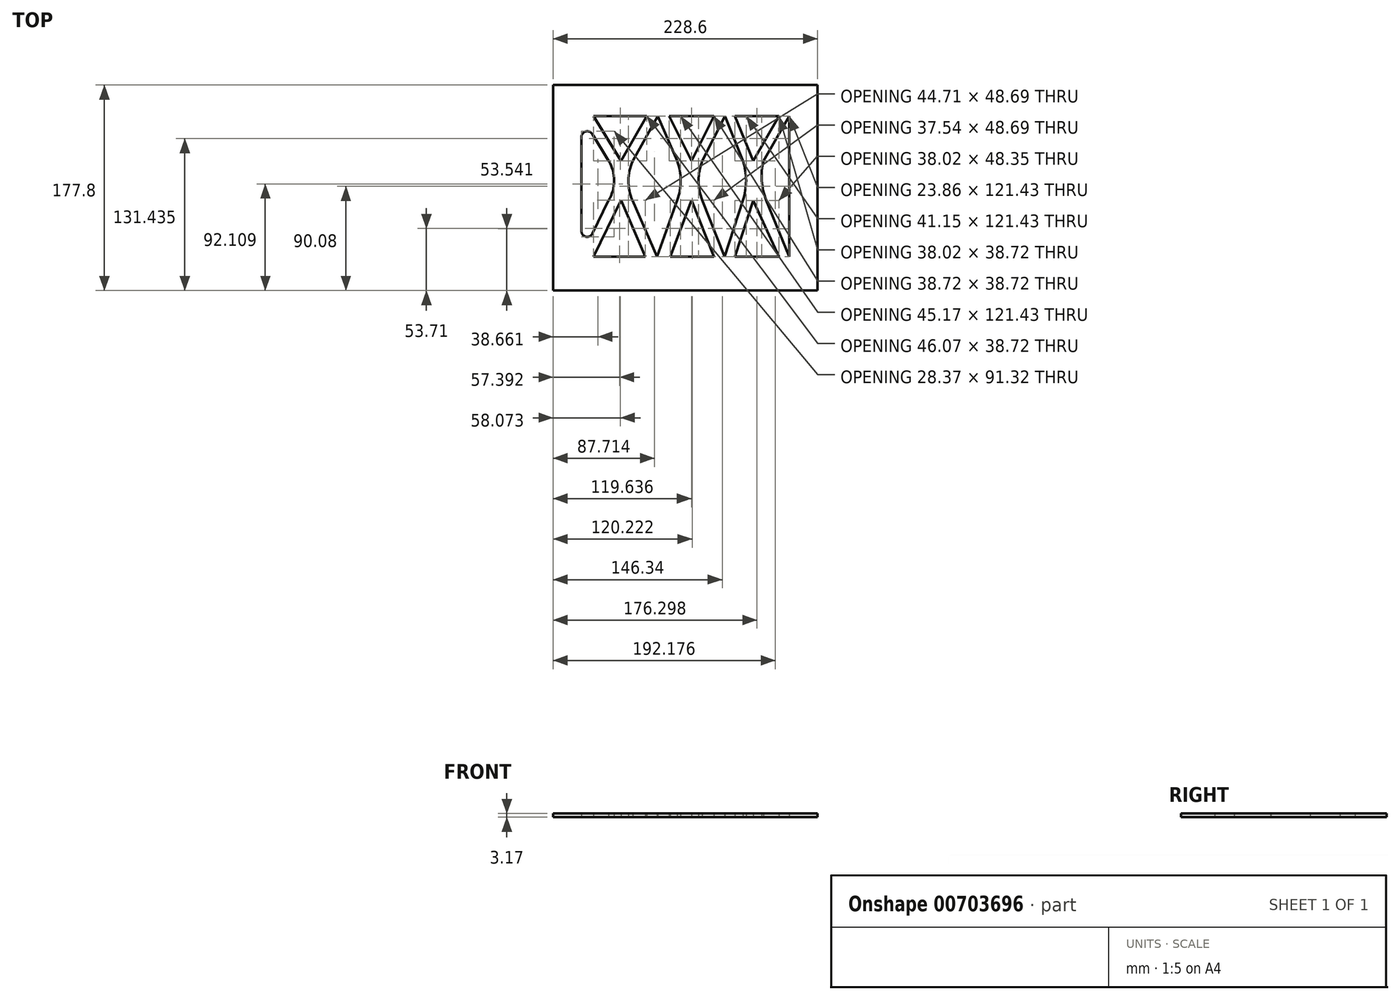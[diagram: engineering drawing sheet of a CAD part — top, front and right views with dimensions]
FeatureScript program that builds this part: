
annotation { "Feature Type Name" : "Feature", "Feature Type Description" : "" }
export const myFeature = defineFeature(function(context is Context, id is Id, definition is map)
    precondition{}
    {
        {
            var Q0;
            Q0=qCreatedBy(makeId("Top.planeOp"),FACE);
            var sketch = newSketch(context, id + "F0", { "sketchPlane" : qUnion([Q0])});
            skLineSegment(sketch, "E0", {"start": v(-115.17, 85) * mm, "end": v(-115.17, -92.8) * mm});
            skLineSegment(sketch, "E1", {"start": v(113.43, -92.8) * mm, "end": v(-115.17, -92.8) * mm});
            skLineSegment(sketch, "E2", {"start": v(113.43, -92.8) * mm, "end": v(113.43, 85) * mm});
            skLineSegment(sketch, "E3", {"start": v(113.43, 85) * mm, "end": v(-115.17, 85) * mm});
            skLineSegment(sketch, "E4", {"start": v(-90.7, 58) * mm, "end": v(-90.7, -63.43) * mm});
            skLineSegment(sketch, "E5", {"start": v(-90.7, -63.43) * mm, "end": v(-67.1, -14.75) * mm});
            skLineSegment(sketch, "E6", {"start": v(-90.7, 58) * mm, "end": v(-67.1, 19.28) * mm});
            skArc(sketch, "E7", {"start": v(-67.1, -14.75) * mm, "mid": v(-62.32, 2.27) * mm, "end": v(-67.1, 19.28) * mm});
            skLineSegment(sketch, "E8", {"start": v(-80.13, -63.43) * mm, "end": v(-56.54, -14.75) * mm});
            skLineSegment(sketch, "E9", {"start": v(-80.13, 58) * mm, "end": v(-56.54, 19.28) * mm});
            skLineSegment(sketch, "E10", {"start": v(-56.54, 19.28) * mm, "end": v(-34.06, 58) * mm});
            skLineSegment(sketch, "E11", {"start": v(-46.32, 19.28) * mm, "end": v(-24.52, 58) * mm});
            skLineSegment(sketch, "E12", {"start": v(-56.54, -14.75) * mm, "end": v(-35.42, -63.43) * mm});
            skPoint(sketch, "E12.endSnap0", {"position": v(-35.42, 38.64) * mm});
            skLineSegment(sketch, "E13", {"start": v(-46.57, -14.75) * mm, "end": v(-25.45, -63.43) * mm});
            skArc(sketch, "E14", {"start": v(-46.32, 19.28) * mm, "mid": v(-50.04, 2.3) * mm, "end": v(-46.57, -14.75) * mm});
            skLineSegment(sketch, "E15", {"start": v(-80.13, 58) * mm, "end": v(-34.06, 58) * mm});
            skLineSegment(sketch, "E16", {"start": v(-80.13, -63.43) * mm, "end": v(-35.42, -63.43) * mm});
            skLineSegment(sketch, "E17", {"start": v(-24.52, 58) * mm, "end": v(-7.85, 19.28) * mm});
            skLineSegment(sketch, "E18", {"start": v(-25.45, -63.43) * mm, "end": v(-7.85, -14.75) * mm});
            skArc(sketch, "E19", {"start": v(-7.85, -14.75) * mm, "mid": v(-4.87, 2.27) * mm, "end": v(-7.85, 19.28) * mm});
            skLineSegment(sketch, "E20", {"start": v(-14.9, 58) * mm, "end": v(4.47, 19.28) * mm});
            skLineSegment(sketch, "E21", {"start": v(-13.72, -63.43) * mm, "end": v(4.47, -14.75) * mm});
            skLineSegment(sketch, "E22", {"start": v(-14.9, 58) * mm, "end": v(23.82, 58) * mm});
            skLineSegment(sketch, "E23", {"start": v(23.82, 58) * mm, "end": v(4.47, 19.28) * mm});
            skLineSegment(sketch, "E24", {"start": v(-13.72, -63.43) * mm, "end": v(23.82, -63.43) * mm});
            skLineSegment(sketch, "E25", {"start": v(23.82, -63.43) * mm, "end": v(4.47, -14.75) * mm});
            skLineSegment(sketch, "E26", {"start": v(33.2, -63.43) * mm, "end": v(13.85, -14.75) * mm});
            skLineSegment(sketch, "E27", {"start": v(33.32, 58) * mm, "end": v(13.85, 19.28) * mm});
            skArc(sketch, "E28", {"start": v(13.85, 19.28) * mm, "mid": v(10.6, 2.27) * mm, "end": v(13.85, -14.75) * mm});
            skLineSegment(sketch, "E29", {"start": v(33.32, 58) * mm, "end": v(49.05, 19.28) * mm});
            skLineSegment(sketch, "E30", {"start": v(42.12, 58) * mm, "end": v(57.85, 19.28) * mm});
            skLineSegment(sketch, "E31", {"start": v(57.85, 19.28) * mm, "end": v(80.14, 58) * mm});
            skLineSegment(sketch, "E32", {"start": v(80.14, 58) * mm, "end": v(42.12, 58) * mm});
            skLineSegment(sketch, "E33", {"start": v(33.2, -63.43) * mm, "end": v(49.05, -14.75) * mm});
            skLineSegment(sketch, "E34", {"start": v(42.12, -63.43) * mm, "end": v(57.85, -15.08) * mm});
            skLineSegment(sketch, "E35", {"start": v(57.85, -15.08) * mm, "end": v(80.14, -63.43) * mm});
            skLineSegment(sketch, "E36", {"start": v(80.14, -63.43) * mm, "end": v(42.12, -63.43) * mm});
            skLineSegment(sketch, "E37", {"start": v(88.94, 58) * mm, "end": v(66.65, 19.28) * mm});
            skLineSegment(sketch, "E38", {"start": v(88.94, -63.43) * mm, "end": v(69.16, -14.75) * mm});
            skArc(sketch, "E39", {"start": v(49.05, -14.75) * mm, "mid": v(51.75, 2.27) * mm, "end": v(49.05, 19.28) * mm});
            skArc(sketch, "E40", {"start": v(66.65, 19.28) * mm, "mid": v(65.22, 2.07) * mm, "end": v(69.16, -14.75) * mm});
            skLineSegment(sketch, "E41", {"start": v(88.94, 58) * mm, "end": v(88.94, -63.43) * mm});
            skSolve(sketch);
        }
        {
            var Q0;
            Q0=makeQuery(id+"F0.imprint","IMPRINT",FACE,{"disambiguationData":[TD([[makeQuery(id+"F0.imprint","IMPRINT",EDGE,{"derivedFrom":sQuery(id+"F0.wireOp",EDGE,"E0")}),1.0]])]});
            extrude(context, id + "F1", {"entities" : qUnion([Q0]), "depth" : 3.17 * mm, "offsetDistance" : 25.4 * mm});
        }
        {
            var Q0;
            Q0=makeQuery(id+"F1.opExtrude","SWEPT_EDGE",EDGE,{"disambiguationData":[OSD([sQuery(id+"F0.wireOp",EDGE,"E4"),sQuery(id+"F0.wireOp",EDGE,"E5")])]});
            var Q1;
            Q1=makeQuery(id+"F1.opExtrude","SWEPT_EDGE",EDGE,{"disambiguationData":[OSD([sQuery(id+"F0.wireOp",EDGE,"E4"),sQuery(id+"F0.wireOp",EDGE,"E6")])]});
            fillet(context, id + "F2", {"entities" : qUnion([Q0, Q1]), "radius" : 5.08 * mm, "tangentPropagation" : true, "allowEdgeOverflow" : false});
        }
    });
